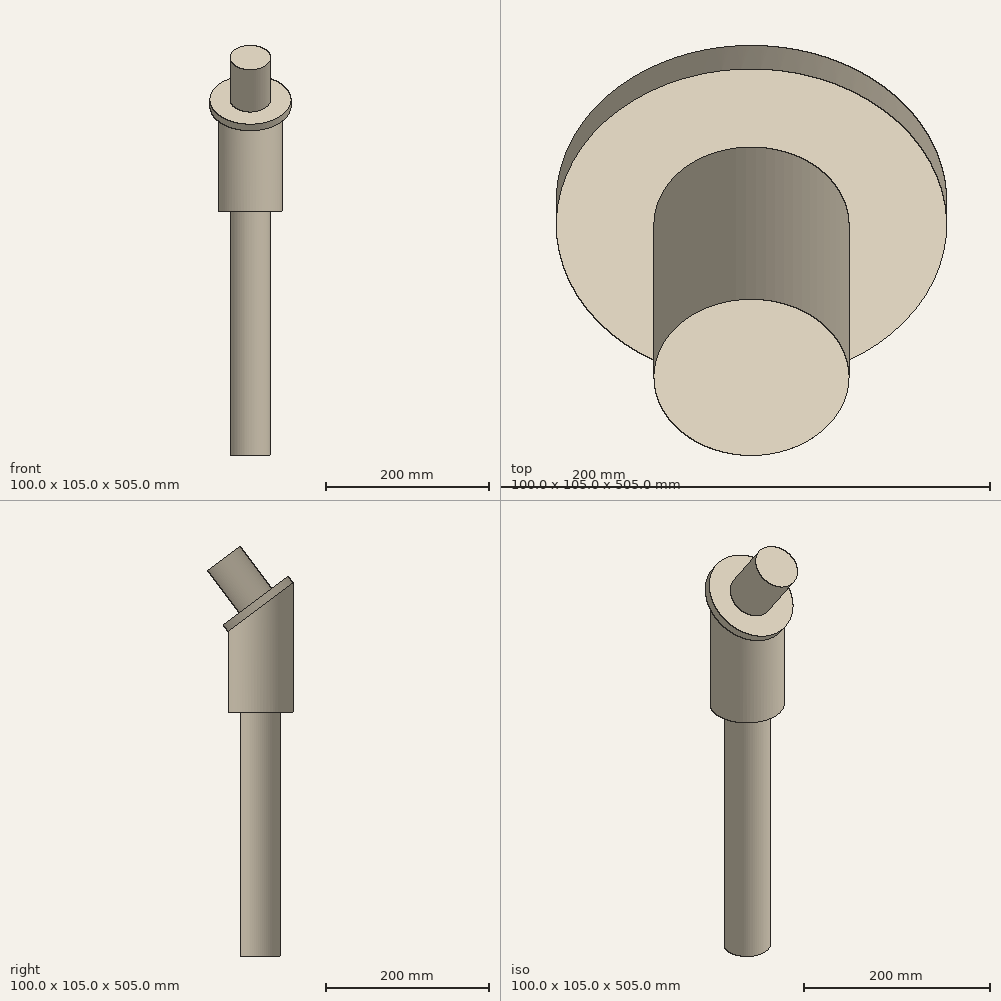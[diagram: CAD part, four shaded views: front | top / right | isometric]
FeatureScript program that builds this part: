
annotation { "Feature Type Name" : "Feature", "Feature Type Description" : "" }
export const myFeature = defineFeature(function(context is Context, id is Id, definition is map)
    precondition{}
    {
        {
            var Q0;
            Q0=qCreatedBy(makeId("Top.planeOp"),FACE);
            var sketch = newSketch(context, id + "F0", { "sketchPlane" : qUnion([Q0])});
            skCircle(sketch, "E0", {"center": v(0, 0) * mm, "radius": 40 * mm});
            skCircle(sketch, "E1", {"center": v(0, 0) * mm, "radius": 25 * mm});
            skSolve(sketch);
        }
        {
            var Q0;
            Q0=makeQuery(id+"F0.imprint","IMPRINT",FACE,{"disambiguationData":[TD([[makeQuery(id+"F0.imprint","IMPRINT",EDGE,{"derivedFrom":sQuery(id+"F0.wireOp",EDGE,"E1")}),1.0]])]});
            extrude(context, id + "F1", {"entities" : qUnion([Q0]), "oppositeDirection" : true, "depth" : 300 * mm, "offsetDistance" : 25 * mm});
        }
        {
            var Q0;
            Q0 = qSketchRegion(id + "F0", true);
            var Q1;
            Q1=makeQuery(id+"F1.opExtrude","CAP_FACE",FACE,{"disambiguationData":[OSD([sQuery(id+"F0.wireOp",EDGE,"E1")])],"isStart":true});
            extrude(context, id + "F2", {"entities" : qUnion([Q0, Q1]), "operationType" : NewBodyOperationType.ADD, "depth" : 100 * mm, "offsetDistance" : 25 * mm});
        }
        {
            var Q0;
            Q0=qCreatedBy(makeId("Right.planeOp"),FACE);
            var sketch = newSketch(context, id + "F3", { "sketchPlane" : qUnion([Q0])});
            skLineSegment(sketch, "E2", {"start": v(0, 100) * mm, "end": v(40, 100) * mm});
            skLineSegment(sketch, "E3", {"start": v(40, 100) * mm, "end": v(40, 160) * mm});
            skLineSegment(sketch, "E4", {"start": v(40, 160) * mm, "end": v(-40, 100) * mm});
            skLineSegment(sketch, "E5", {"start": v(-40, 100) * mm, "end": v(0, 100) * mm});
            skSolve(sketch);
        }
        {
            var Q0;
            Q0 = qSketchRegion(id + "F3", true);
            var Q1;
            Q1=makeQuery(id+"F2.opExtrude","SWEPT_FACE",FACE,{"disambiguationData":[OSD([sQuery(id+"F0.wireOp",EDGE,"E0")])]});
            var Q2;
            Q2=makeQuery(id+"F2.opExtrude","SWEPT_FACE",FACE,{"disambiguationData":[OSD([sQuery(id+"F0.wireOp",EDGE,"E0")])]});
            extrude(context, id + "F4", {"entities" : qUnion([Q0]), "operationType" : NewBodyOperationType.ADD, "endBound" : BoundingType.UP_TO_SURFACE, "depth" : 25 * mm, "endBoundEntityFace" : qUnion([Q1]), "offsetDistance" : 25 * mm, "hasSecondDirection" : true, "secondDirectionBound" : SecondDirectionBoundingType.UP_TO_SURFACE, "secondDirectionOppositeDirection" : true, "secondDirectionDepth" : 25 * mm, "secondDirectionBoundEntityFace" : qUnion([Q2])});
        }
        {
            var Q0;
            Q0=makeQuery(id+"F4.opExtrude","SWEPT_FACE",FACE,{"disambiguationData":[OSD([sQuery(id+"F3.wireOp",EDGE,"E4")])]});
            var sketch = newSketch(context, id + "F5", { "sketchPlane" : qUnion([Q0])});
            skCircle(sketch, "E6", {"center": v(0, 78) * mm, "radius": 50 * mm});
            skSolve(sketch);
        }
        {
            var Q0;
            Q0 = qSketchRegion(id + "F5", true);
            extrude(context, id + "F6", {"entities" : qUnion([Q0]), "operationType" : NewBodyOperationType.ADD, "depth" : 10 * mm, "offsetDistance" : 25 * mm});
        }
        {
            var Q0;
            Q0=makeQuery(id+"F6.opExtrude","CAP_FACE",FACE,{"disambiguationData":[OSD([sQuery(id+"F5.wireOp",EDGE,"E6")])],"isStart":false});
            var sketch = newSketch(context, id + "F7", { "sketchPlane" : qUnion([Q0])});
            skCircle(sketch, "E7", {"center": v(0, 78) * mm, "radius": 25 * mm});
            skSolve(sketch);
        }
        {
            var Q0;
            Q0 = qSketchRegion(id + "F7", true);
            extrude(context, id + "F8", {"entities" : qUnion([Q0]), "operationType" : NewBodyOperationType.ADD, "depth" : 65 * mm, "offsetDistance" : 25 * mm});
        }
    });
